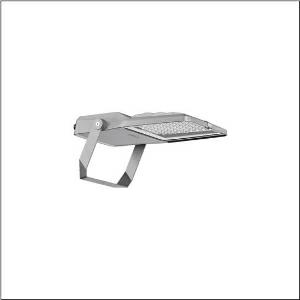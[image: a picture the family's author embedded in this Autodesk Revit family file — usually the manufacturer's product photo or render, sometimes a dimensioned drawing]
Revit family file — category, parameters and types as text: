
# Revit family: floodlight_fl_21_iq_mini___pl43_5xa7772b4a1a_cc8f
name_source: partatom
category: Lighting Fixtures
units: mm (PartAtom-declared; Revit-internal decimal feet)

## family parameters
Cut with Voids When Loaded = No
Host = Face
Light Source = No
Part Type = Normal
Room Calculation Point = No
Round Connector Dimension = Use Diameter
Shared = No

## types (1)
- --- (1 x LED, 6660 lm, 45.5 W, 4000K)
    Apparent Load = 46 VA
    CIE Flux Codes = 27 78 99 100 100
    Color Rendering = 70
    Color Temperature = 4000K
    Default Elevation = 1800 mm
    Description = Floodlight FL 21 iQ mini, floodlight, primary light control with lens, of PMMA, primary optical cover: protective disc, of toughened safety glass, transparent, light distribution: PL43, light emission: direct distribution, installation type: surface-mounted, LED, High Power LED, rated luminous flux: 6.660lm, luminous efficacy: 146lm/W, light colour: 740, colour temperature: 4000K, control gear: iQ Street-Remote/DALI, control: Street-Remote, Auto-Match, Temp-Guard, Night-Set, Smart-Wire, Desk-Remote (wireless, voltage-free reading and setting of iQ features in the workshop via application-optimized NFC function/RFID function), optimised constant luminous flux control (CLO 2.0), with terminal, 6-pole, mains connection: 220..240V, AC, 50/60Hz, start of lifetime: 46W, end of service life: 48W, reduction: 22W, luminaire housing, of diecast aluminium, powder-coated, Siteco® metallic grey (DB 702S), corrosivity category C5 mid according to DIN EN ISO 12944, suitable for swimming pools, chlorine-resistant, sealing non-destructively replaceable, mounting bracket, of steel, galvanised, powder-coated, Siteco® metallic grey (DB 702S), protection rating (complete): IP66, insulation class (complete): insulation class II (safety insulation), certification: CE, ENEC, VDE, protection symbol: D, impact resistance: IK08, permissible operating ambient temperature: -40..+40°C, permissible operating ambient temperature for outdoor applications: -40..+50°C, standard: DIN EN 12944, LABS conformity tested according to VDMA 24364:2018-05, packaging unit: 1 piece

Light Distribution: PL43
    Height = 70 mm
    Lamp = 1 x LED
    Lamp Light Flux = 6660 lm
    Lamp Power = 45.5 W
    Lamp count = 1
    Length = 485 mm
    Luminous efficacy = 146 lm/W
    Manufacturer = Siteco
    ModVariant = No
    Model = 5XA7772B4A1A
    Number of Poles = 1
    OnlyDefault = Yes
    Power Factor = 1
    Product Name = Floodlight FL 21 iQ mini | PL43
    Product group = floodlight | pylon annexe
    ProductGroupID = 6200
    Protection Class = Protection class II
    Protection Degree = IP 66
    RLX_Detail_Level = 1
    RLX_Emergency_Light_Flux = 0 lm
    RLX_Emergency_Type = 0
    RLX_Emergency_Type_DB = No
    RlxData = <blob elided: 96085 chars, md5=1e79ec65>
    Socket = socket
    Standby Power = 0 W
    System Light Flux = 6660 lm
    System Power = 46 W
    Type Comments = factory setting: luminous flux: 100 % | dim-lin: 254 | 463 mA
    Type Image = l_1006845.jpg
    URL = http://relux.com
    VarID = @adj_161978
    Voltage = 0 V
    Weight = 0.00 kg
    Width = 337 mm

## geometry (parser evidence)
native form markers: Blend x4, Sweep x13
no freeform markers — native parametric forms only
